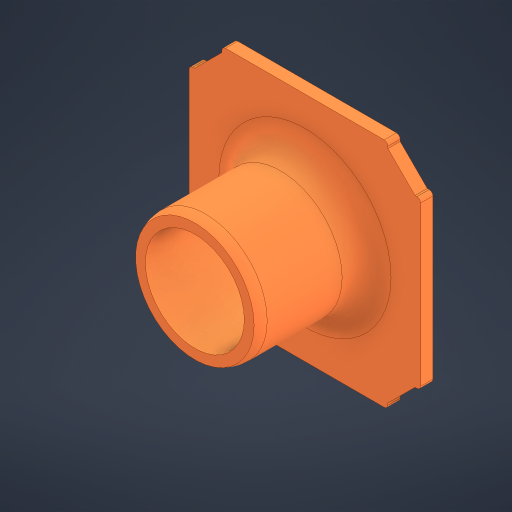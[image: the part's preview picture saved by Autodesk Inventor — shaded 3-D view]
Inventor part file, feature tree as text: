
AUTODESK INVENTOR PART (.ipt)
format: ipt  version: 2023.4 (Build 274418000, 418)  size: 302,592 bytes
history: native  units: mm
features: extrude x3, other x3, fillet x2, plane x1, chamfer x1, reference x1, projected_geometry x1
ambient origin geometry x8: Origin, YZ Plane, XZ Plane, XY Plane, X Axis, Y Axis, Z Axis, Center Point
bodies: Solid1 (feature_tree)
feature tree (12):
  plane  "Work Plane1"
  extrude  "Extrusion1"  Depth=0.075mm
  extrude  "Extrusion2"  Depth=2.5mm TaperAngle=0.0deg
  extrude  "Extrusion3"  Depth=10.0mm
  chamfer  "Chamfer1"  Distance=10.0mm
  fillet  "Fillet1"  Radius=5.0mm
  fillet  "Fillet2"  Radius=5.0mm
  reference  "Reference1"
  projected_geometry  "Projected Loop1"
  other  "<path>\Projects\Project Protocube\Protocube\CAD, STL, OBJ Files\1 CAD\Cube 1x1 V5.iam"
  other  "Cube 1x1 V5.iam"
  other  "Cube 1x1 Bottom V5:1"
note: 1 file-system path scrubbed to <path> (originals preserved in map.json)
